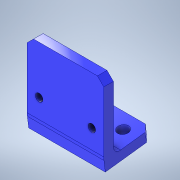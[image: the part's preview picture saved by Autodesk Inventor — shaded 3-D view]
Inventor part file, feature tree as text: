
AUTODESK INVENTOR PART (.ipt)
format: ipt  version: 2022.6 (Build 266554000, 554)  size: 220,672 bytes
history: native  units: mm
features: sketch x8, extrude x4, plane x2, hole x2, fillet x2, chamfer x1, other x1, rib x1, projected_geometry x1
ambient origin geometry x8: Origin, YZ Plane, XZ Plane, XY Plane, X Axis, Y Axis, Z Axis, Center Point
bodies: Solid1 (feature_tree)
feature tree (22):
  extrude  "Extrusion1"  Depth=24.0mm
  plane  "Work Plane1"
  plane  "Work Plane2"
  sketch  "Sketch2"  dims[d2=3.0mm d3=0.0mm d9=12.0mm d10=23.0mm]
  extrude  "Extrusion4"  Depth=3.0mm
  extrude  "Extrusion5"  Depth=24.0mm
  hole  "Hole3"  [1 undecoded]
  chamfer  "Chamfer1"  Distance=15.0mm
  sketch  "Sketch11"  dims[d56=4.5mm]
  extrude  "Extrusion7"  Depth=15.0mm
  hole  "Hole4"  [1 undecoded]
  other  "Bend Part1"
  fillet  "Fillet1"  Radius=2.4mm
  rib  "Rib3"
  fillet  "Fillet2"  Radius=15.0mm
  sketch  "Sketch1"  dims[d0=24.0mm d1=20.0mm]
  sketch  "Sketch5"  dims[d47=0.0mm d48=24.0mm]
  sketch  "Sketch6"  dims[d49=5.0mm d50=0.0mm d51=3.0mm d52=15.0mm d53=0.0mm]
  sketch  "Sketch7"  dims[d54=15.0mm d55=4.5mm]
  projected_geometry  "Projected Loop6"
  sketch  "Sketch13"  dims[d57=3.4mm d58=6.0mm d59=4.0mm d60=2.0mm d61=90.0deg d62=8.0mm d63=20.594885mm d65=2.0mm d66=2.0mm d67=45.0deg d88=2.4mm d89=15.0mm]
  sketch  "Sketch15"  dims[d91=16.5mm d92=4.0mm d93=3.0mm d94=0.0mm d95=5.0mm d96=2.0mm d97=2.4mm d98=6.0mm d99=6.5mm d100=1.3mm d101=90.0deg d102=8.0mm d103=20.594885mm d105=1.0mm d106=5.0mm d107=1.22173mm d116=2.0mm d117=9.0mm d118=30.0deg d119=1.0mm d120=2.0mm d121=0.0mm d122=0.0mm d123=1.0mm d124=1.0mm d125=2.0mm]
note: 2 required parameter values undecoded (feature->parameter linkage not recoverable at this tier; creation-order binding heuristic only, values carry confidence <= 0.55)
